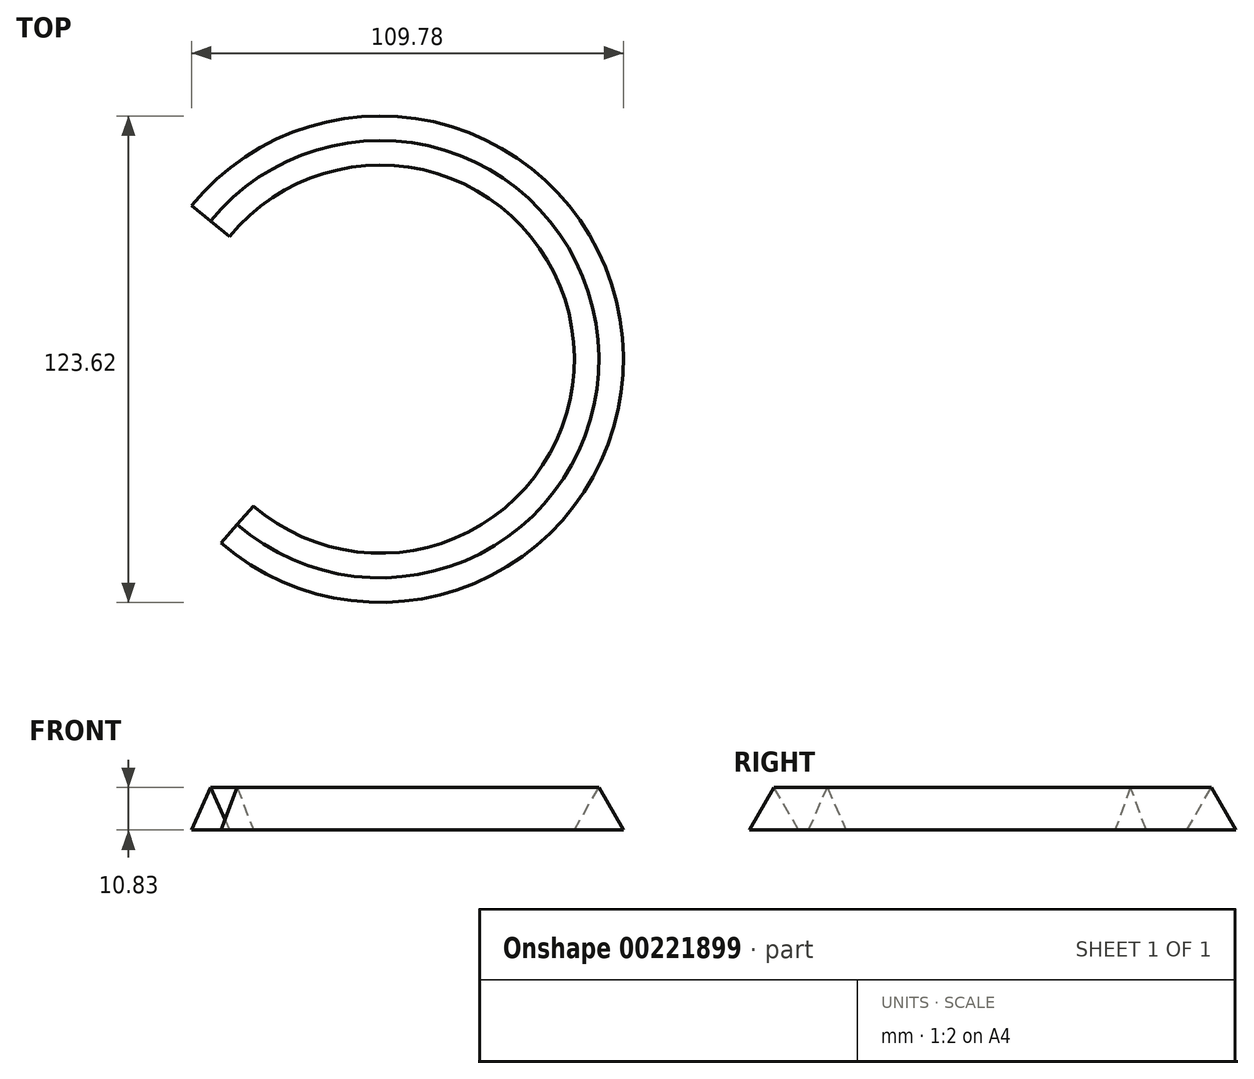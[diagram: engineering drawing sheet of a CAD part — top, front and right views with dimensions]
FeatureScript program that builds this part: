
annotation { "Feature Type Name" : "Feature", "Feature Type Description" : "" }
export const myFeature = defineFeature(function(context is Context, id is Id, definition is map)
    precondition{}
    {
        {
            var Q0;
            Q0=qCreatedBy(makeId("Top.planeOp"),FACE);
            var sketch = newSketch(context, id + "F0", { "sketchPlane" : qUnion([Q0])});
            skArc(sketch, "E0", {"start": v(-39.68, -30.82) * mm, "mid": v(51.99, 16.09) * mm, "end": v(-46.47, 46.24) * mm});
            skSolve(sketch);
        }
        {
            var Q0;
            Q0=sQuery(id+"F0.wireOp",VERTEX,"E0.start");
            var Q1;
            Q1=sQuery(id+"F0.wireOp",EDGE,"E0");
            cPlane(context, id + "F1", {"entities" : qUnion([Q0, Q1]), "cplaneType" : CPlaneType.CURVE_POINT, "offset" : 25.4 * mm, "width" : 152.4 * mm, "height" : 152.4 * mm});
        }
        {
            var Q0;
            Q0=qCreatedBy(id+"F1.planeOp",FACE);
            var sketch = newSketch(context, id + "F2", { "sketchPlane" : qUnion([Q0])});
            skCircle(sketch, "E1.cCircle", {"center": v(-49.27, 0) * mm, "radius": 3.6 * mm, "construction": true});
            skLineSegment(sketch, "E1.0", {"start": v(-49.27, 7.22) * mm, "end": v(-43.02, -3.6) * mm});
            skLineSegment(sketch, "E1.1", {"start": v(-43.02, -3.6) * mm, "end": v(-55.52, -3.6) * mm});
            skLineSegment(sketch, "E1.2", {"start": v(-55.52, -3.6) * mm, "end": v(-49.27, 7.22) * mm});
            skPoint(sketch, "E1.0.midPoint", {"position": v(-46.14, 1.8) * mm});
            skSolve(sketch);
        }
        {
            var Q0;
            Q0 = qSketchRegion(id + "F2", true);
            var Q1;
            Q1=sQuery(id+"F0.wireOp",EDGE,"E0");
            sweep(context, id + "F3", {"profiles" : qUnion([Q0]), "path" : qUnion([Q1])});
        }
    });
